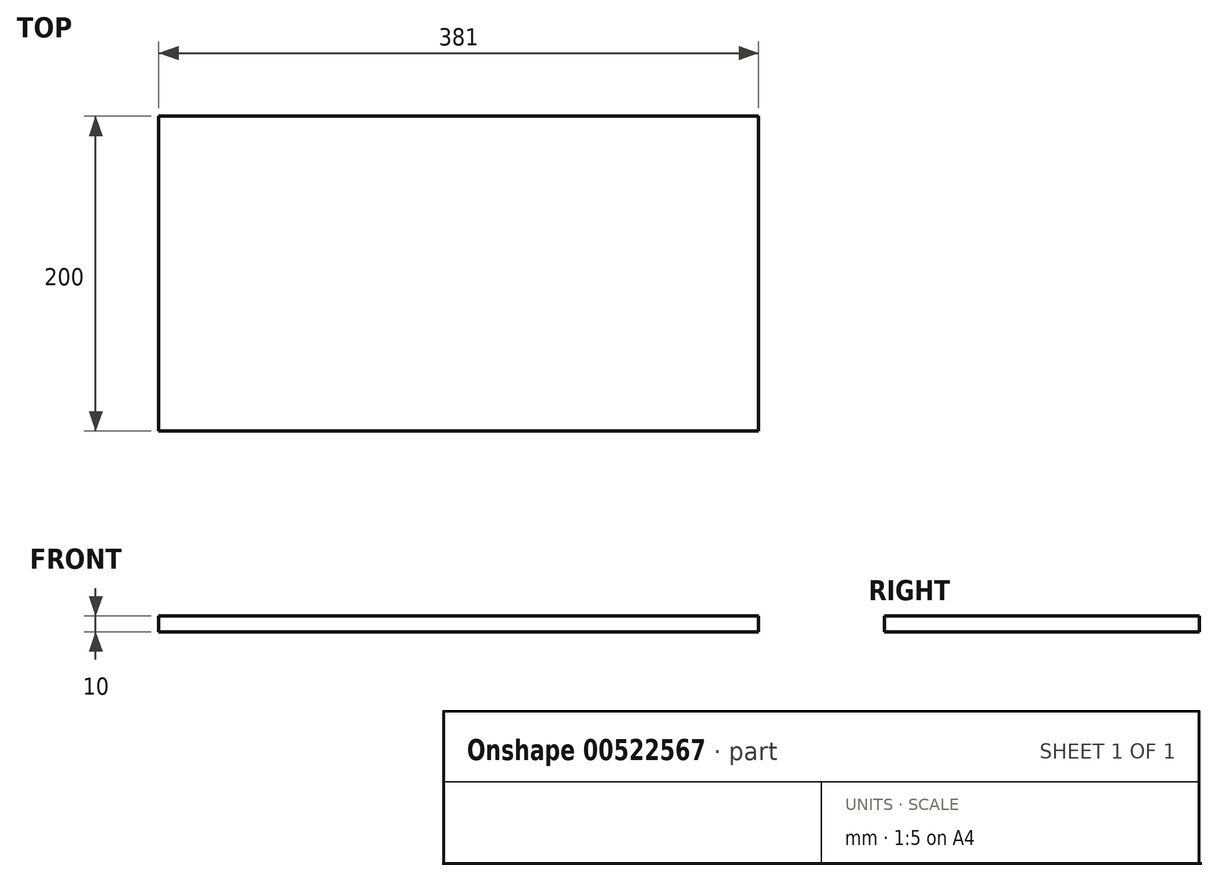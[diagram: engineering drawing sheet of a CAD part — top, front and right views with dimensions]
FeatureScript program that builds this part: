
annotation { "Feature Type Name" : "Feature", "Feature Type Description" : "" }
export const myFeature = defineFeature(function(context is Context, id is Id, definition is map)
    precondition{}
    {
        {
            var Q0;
            Q0=qCreatedBy(makeId("Top.planeOp"),FACE);
            var sketch = newSketch(context, id + "F0", { "sketchPlane" : qUnion([Q0])});
            skLineSegment(sketch, "E0.bottom", {"start": v(-401.5, 61.16) * mm, "end": v(-20.5, 61.16) * mm});
            skLineSegment(sketch, "E0.top", {"start": v(-401.5, -138.84) * mm, "end": v(-20.5, -138.84) * mm});
            skLineSegment(sketch, "E0.left", {"start": v(-401.5, 61.16) * mm, "end": v(-401.5, -138.84) * mm});
            skLineSegment(sketch, "E0.right", {"start": v(-20.5, 61.16) * mm, "end": v(-20.5, -138.84) * mm});
            skSolve(sketch);
        }
        {
            var Q0;
            Q0 = qSketchRegion(id + "F0", true);
            extrude(context, id + "F1", {"entities" : qUnion([Q0]), "depth" : 10 * mm, "offsetDistance" : 25 * mm});
        }
    });
